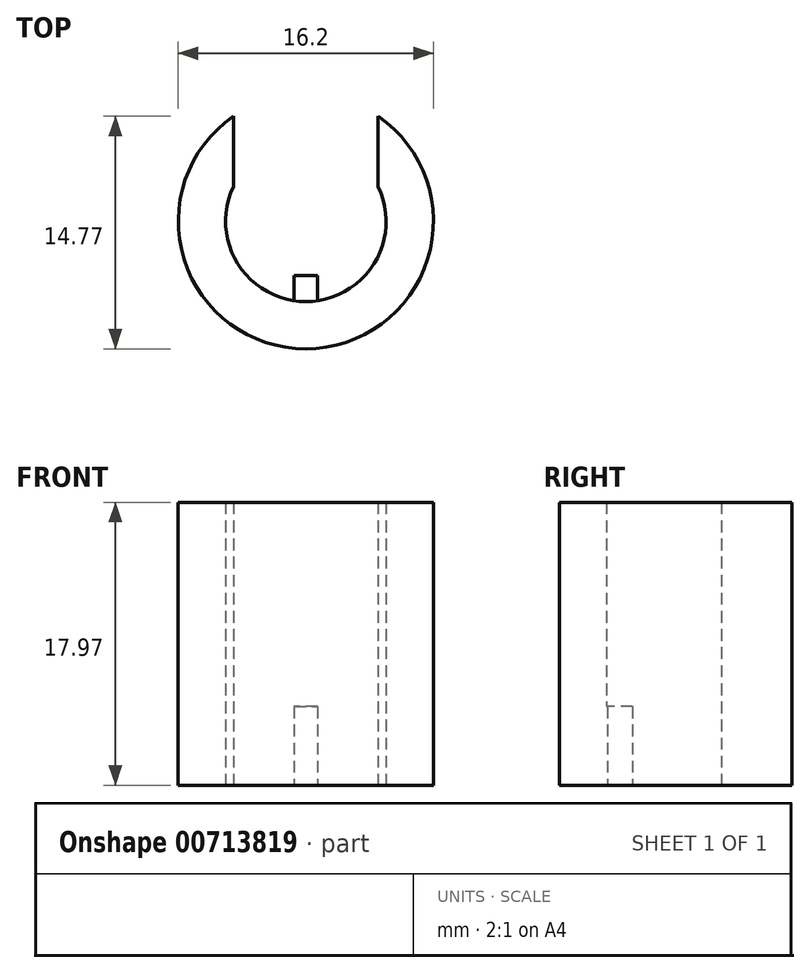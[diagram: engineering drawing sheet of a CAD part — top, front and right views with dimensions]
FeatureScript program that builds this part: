
annotation { "Feature Type Name" : "Feature", "Feature Type Description" : "" }
export const myFeature = defineFeature(function(context is Context, id is Id, definition is map)
    precondition{}
    {
        {
            var Q0;
            Q0=qCreatedBy(makeId("Top.planeOp"),FACE);
            var sketch = newSketch(context, id + "F0", { "sketchPlane" : qUnion([Q0])});
            skCircle(sketch, "E0", {"center": v(0, 0) * mm, "radius": 5.1 * mm});
            skCircle(sketch, "E1", {"center": v(0, 0) * mm, "radius": 8.1 * mm});
            skSolve(sketch);
        }
        {
            var Q0;
            Q0=makeQuery(id+"F0.imprint","IMPRINT",FACE,{"disambiguationData":[TD([[makeQuery(id+"F0.imprint","IMPRINT",EDGE,{"derivedFrom":sQuery(id+"F0.wireOp",EDGE,"E0")}),-1.0]])]});
            extrude(context, id + "F1", {"entities" : qUnion([Q0]), "depth" : 17.97 * mm, "offsetDistance" : 25 * mm});
        }
        {
            var Q0;
            Q0=qCreatedBy(makeId("Front.planeOp"),FACE);
            cPlane(context, id + "F2", {"entities" : qUnion([Q0]), "cplaneType" : CPlaneType.OFFSET, "offset" : 9.1 * mm, "oppositeDirection" : true, "width" : 150 * mm, "height" : 150 * mm});
        }
        {
            var Q0;
            Q0=qCreatedBy(id+"F2.planeOp",FACE);
            var sketch = newSketch(context, id + "F3", { "sketchPlane" : qUnion([Q0])});
            skLineSegment(sketch, "E2", {"start": v(4.6, 17.97) * mm, "end": v(0, 17.97) * mm});
            skLineSegment(sketch, "E3", {"start": v(0, 17.97) * mm, "end": v(-4.6, 17.97) * mm});
            skLineSegment(sketch, "E4", {"start": v(-4.6, 17.97) * mm, "end": v(-4.6, 0) * mm});
            skLineSegment(sketch, "E5", {"start": v(-4.6, 0) * mm, "end": v(0, 0) * mm});
            skLineSegment(sketch, "E6", {"start": v(0, 0) * mm, "end": v(4.6, 0) * mm});
            skLineSegment(sketch, "E7", {"start": v(4.6, 0) * mm, "end": v(4.6, 17.97) * mm});
            skSolve(sketch);
        }
        {
            var Q0;
            Q0=makeQuery(id+"F3.imprint","IMPRINT",FACE,{"disambiguationData":[TD([[makeQuery(id+"F3.imprint","IMPRINT",EDGE,{"derivedFrom":sQuery(id+"F3.wireOp",EDGE,"E2")}),1.0]])]});
            extrude(context, id + "F4", {"entities" : qUnion([Q0]), "operationType" : NewBodyOperationType.REMOVE, "depth" : 7.6 * mm, "offsetDistance" : 25 * mm, "hasSecondDirection" : true, "secondDirectionOppositeDirection" : true, "secondDirectionDepth" : 0.4 * mm});
        }
        {
            var Q0;
            {var subQ0=sQuery(id+"F0.wireOp",EDGE,"E0");var subQ1=sQuery(id+"F0.wireOp",EDGE,"E1");Q0=makeQuery(id+"F4.boolean.opBoolean","SPLIT",FACE,{"disambiguationData":[TD([makeQuery(id+"F1.opExtrude","SWEPT_FACE",FACE,{"disambiguationData":[OSD([subQ0])]})])],"derivedFrom":makeQuery(id+"F1.opExtrude","CAP_FACE",FACE,{"disambiguationData":[OSD([subQ0,subQ1])],"isStart":true})});}
            var sketch = newSketch(context, id + "F5", { "sketchPlane" : qUnion([Q0])});
            skLineSegment(sketch, "E8", {"start": v(-0.75, 5.04) * mm, "end": v(0, 5.04) * mm});
            skPoint(sketch, "E8.endSnap0", {"position": v(0, 5.1) * mm});
            skLineSegment(sketch, "E9", {"start": v(0, 5.04) * mm, "end": v(0.75, 5.04) * mm});
            skLineSegment(sketch, "E10", {"start": v(0.75, 5.04) * mm, "end": v(0.75, 3.44) * mm});
            skLineSegment(sketch, "E11", {"start": v(0.75, 3.44) * mm, "end": v(0, 3.44) * mm});
            skLineSegment(sketch, "E12", {"start": v(0, 3.44) * mm, "end": v(-0.75, 3.44) * mm});
            skLineSegment(sketch, "E13", {"start": v(-0.75, 3.44) * mm, "end": v(-0.75, 5.04) * mm});
            skSolve(sketch);
        }
        {
            var Q0;
            Q0=makeQuery(id+"F5.imprint","IMPRINT",FACE,{"disambiguationData":[TD([[makeQuery(id+"F5.imprint","IMPRINT",EDGE,{"derivedFrom":sQuery(id+"F5.wireOp",EDGE,"E8")}),-1.0]])]});
            var Q1;
            {var subQ0=sQuery(id+"F5.wireOp",EDGE,"E8");Q1=makeQuery(id+"F5.imprint","IMPRINT",FACE,{"disambiguationData":[TD([[makeQuery(id+"F5.imprint","IMPRINT",EDGE,{"derivedFrom":subQ0}),1.0]])]});}
            extrude(context, id + "F6", {"entities" : qUnion([Q0, Q1]), "operationType" : NewBodyOperationType.ADD, "oppositeDirection" : true, "depth" : 5 * mm, "offsetDistance" : 25 * mm});
        }
    });
